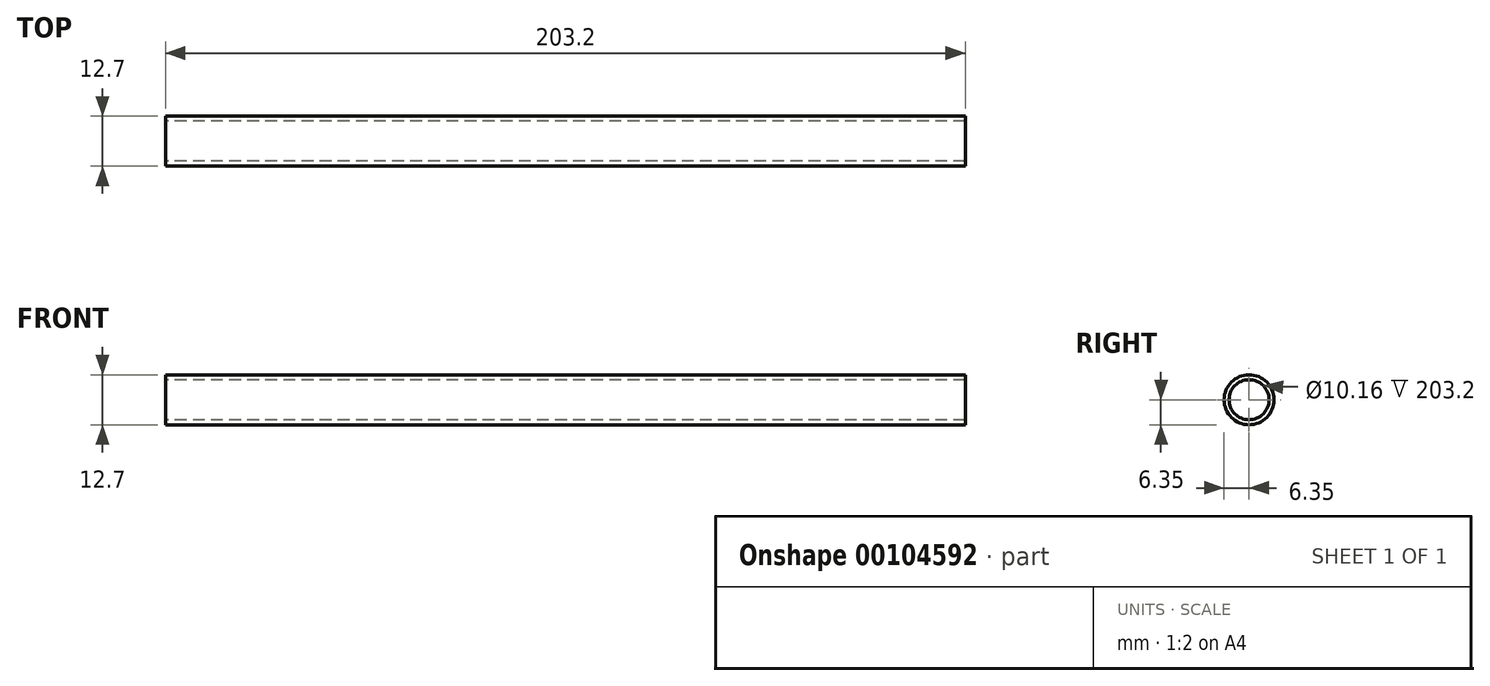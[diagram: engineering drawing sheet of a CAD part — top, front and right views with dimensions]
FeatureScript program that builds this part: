
annotation { "Feature Type Name" : "Feature", "Feature Type Description" : "" }
export const myFeature = defineFeature(function(context is Context, id is Id, definition is map)
    precondition{}
    {
        {
            var Q0;
            Q0=qCreatedBy(makeId("Right.planeOp"),FACE);
            var sketch = newSketch(context, id + "F0", { "sketchPlane" : qUnion([Q0])});
            skCircle(sketch, "E0", {"center": v(0, 0) * mm, "radius": 6.35 * mm});
            skCircle(sketch, "E1", {"center": v(0, 0) * mm, "radius": 5.08 * mm});
            skSolve(sketch);
        }
        {
            var Q0;
            Q0=qCreatedBy(makeId("Front.planeOp"),FACE);
            var sketch = newSketch(context, id + "F1", { "sketchPlane" : qUnion([Q0])});
            skLineSegment(sketch, "E2", {"start": v(0, 0) * mm, "end": v(-203.2, 0) * mm});
            skSolve(sketch);
        }
        {
            var Q0;
            Q0=makeQuery(id+"F0.imprint","IMPRINT",FACE,{"disambiguationData":[TD([[makeQuery(id+"F0.imprint","IMPRINT",EDGE,{"derivedFrom":sQuery(id+"F0.wireOp",EDGE,"E0")}),1.0]])]});
            var Q1;
            Q1=sQuery(id+"F1.wireOp",EDGE,"E2");
            sweep(context, id + "F2", {"profiles" : qUnion([Q0]), "path" : qUnion([Q1])});
        }
    });
